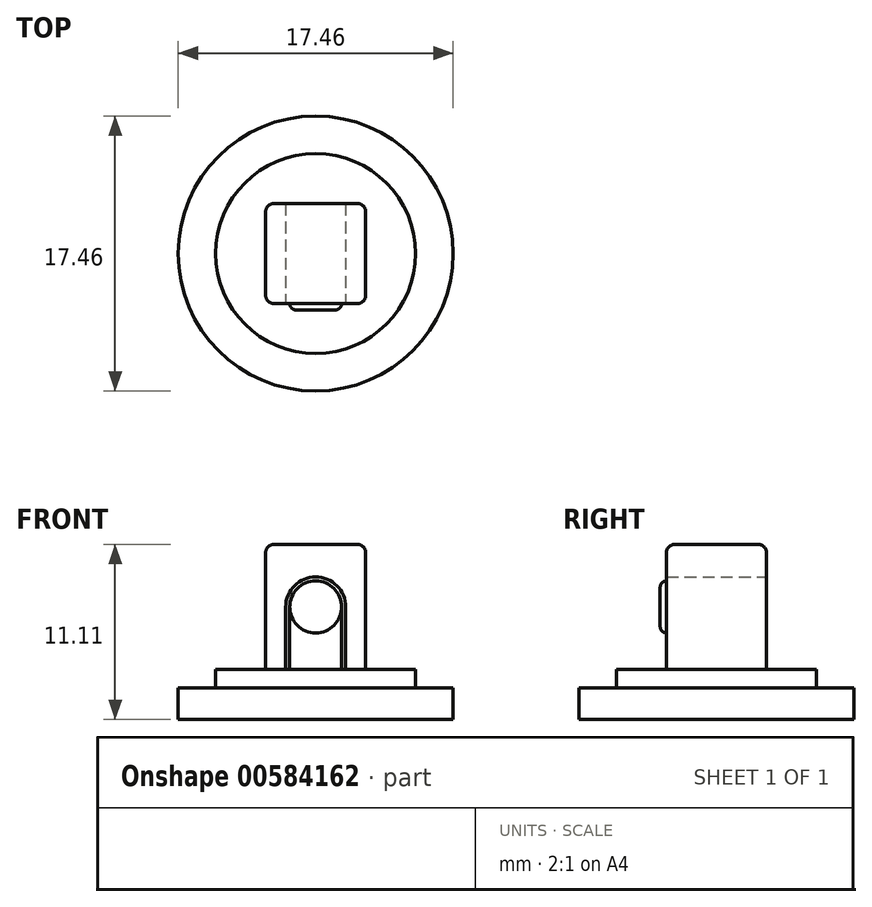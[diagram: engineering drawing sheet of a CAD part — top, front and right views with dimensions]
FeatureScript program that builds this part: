
annotation { "Feature Type Name" : "Feature", "Feature Type Description" : "" }
export const myFeature = defineFeature(function(context is Context, id is Id, definition is map)
    precondition{}
    {
        {
            var Q0;
            Q0=qCreatedBy(makeId("Top.planeOp"),FACE);
            var sketch = newSketch(context, id + "F0", { "sketchPlane" : qUnion([Q0])});
            skCircle(sketch, "E0", {"center": v(0, 0) * mm, "radius": 8.73 * mm});
            skSolve(sketch);
        }
        {
            var Q0;
            Q0=qSketchRegion(id+"F0",true);
            extrude(context, id + "F1", {"entities" : qUnion([Q0]), "depth" : 1.98 * mm, "offsetDistance" : 25.4 * mm});
        }
        {
            var Q0;
            Q0=makeQuery(id+"F1.opExtrude","CAP_FACE",FACE,{"disambiguationData":[OSD([sQuery(id+"F0.wireOp",EDGE,"E0")])],"isStart":false});
            var sketch = newSketch(context, id + "F2", { "sketchPlane" : qUnion([Q0])});
            skCircle(sketch, "E1", {"center": v(0, 0) * mm, "radius": 6.35 * mm});
            skSolve(sketch);
        }
        {
            var Q0;
            Q0=qSketchRegion(id+"F2",true);
            extrude(context, id + "F3", {"entities" : qUnion([Q0]), "operationType" : NewBodyOperationType.ADD, "depth" : 1.2 * mm, "offsetDistance" : 25.4 * mm});
        }
        {
            var Q0;
            Q0=makeQuery(id+"F3.opExtrude","CAP_FACE",FACE,{"disambiguationData":[OSD([sQuery(id+"F2.wireOp",EDGE,"E1")])],"isStart":false});
            var sketch = newSketch(context, id + "F4", { "sketchPlane" : qUnion([Q0])});
            skLineSegment(sketch, "E2.bottom", {"start": v(3.18, 3.18) * mm, "end": v(-3.18, 3.18) * mm});
            skLineSegment(sketch, "E2.top", {"start": v(3.18, -3.18) * mm, "end": v(-3.18, -3.18) * mm});
            skLineSegment(sketch, "E2.left", {"start": v(3.18, 3.18) * mm, "end": v(3.18, -3.18) * mm});
            skLineSegment(sketch, "E2.right", {"start": v(-3.18, 3.18) * mm, "end": v(-3.18, -3.18) * mm});
            skPoint(sketch, "E2.middle", {"position": v(0, 0) * mm});
            skSolve(sketch);
        }
        {
            var Q0;
            Q0=qSketchRegion(id+"F4",true);
            extrude(context, id + "F5", {"entities" : qUnion([Q0]), "operationType" : NewBodyOperationType.ADD, "depth" : 7.94 * mm, "offsetDistance" : 25.4 * mm});
        }
        {
            var Q0;
            Q0=qCreatedBy(makeId("Front.planeOp"),FACE);
            var sketch = newSketch(context, id + "F6", { "sketchPlane" : qUnion([Q0])});
            skCircle(sketch, "E3", {"center": v(0, 7.14) * mm, "radius": 1.9 * mm});
            skSolve(sketch);
        }
        {
            var Q0;
            Q0=qSketchRegion(id+"F6",true);
            extrude(context, id + "F7", {"entities" : qUnion([Q0]), "operationType" : NewBodyOperationType.REMOVE, "endBound" : BoundingType.THROUGH_ALL, "depth" : 25.4 * mm, "offsetDistance" : 25.4 * mm, "hasSecondDirection" : true, "secondDirectionBound" : SecondDirectionBoundingType.THROUGH_ALL, "secondDirectionOppositeDirection" : true, "secondDirectionDepth" : 25.4 * mm});
        }
        {
            var Q0;
            Q0=makeQuery(id+"F5.opExtrude","SWEPT_FACE",FACE,{"disambiguationData":[OSD([sQuery(id+"F4.wireOp",EDGE,"E2.top")])]});
            var sketch = newSketch(context, id + "F8", { "sketchPlane" : qUnion([Q0])});
            skLineSegment(sketch, "E4.bottom", {"start": v(-1.9, 3.17) * mm, "end": v(1.9, 3.17) * mm});
            skLineSegment(sketch, "E4.left", {"start": v(-1.9, 3.18) * mm, "end": v(-1.9, 7.14) * mm});
            skLineSegment(sketch, "E4.right", {"start": v(1.9, 3.18) * mm, "end": v(1.9, 7.14) * mm});
            skLineSegment(sketch, "E5", {"start": v(-1.9, 7.14) * mm, "end": v(1.9, 7.14) * mm});
            skSolve(sketch);
        }
        {
            var Q0;
            Q0=qSketchRegion(id+"F8",true);
            extrude(context, id + "F9", {"entities" : qUnion([Q0]), "operationType" : NewBodyOperationType.REMOVE, "endBound" : BoundingType.THROUGH_ALL, "oppositeDirection" : true, "depth" : 25.4 * mm, "offsetDistance" : 25.4 * mm});
        }
        {
            var Q0;
            Q0=makeQuery(id+"F5.opExtrude","SWEPT_FACE",FACE,{"disambiguationData":[OSD([sQuery(id+"F4.wireOp",EDGE,"E2.top")])]});
            var sketch = newSketch(context, id + "F10", { "sketchPlane" : qUnion([Q0])});
            skArc(sketch, "E6", {"start": v(1.65, 7.14) * mm, "mid": v(0, 8.8) * mm, "end": v(-1.65, 7.14) * mm});
            skLineSegment(sketch, "E7.bottom", {"start": v(-1.65, 3.17) * mm, "end": v(1.65, 3.17) * mm});
            skLineSegment(sketch, "E7.left", {"start": v(-1.65, 3.18) * mm, "end": v(-1.65, 7.14) * mm});
            skLineSegment(sketch, "E7.right", {"start": v(1.65, 3.18) * mm, "end": v(1.65, 7.14) * mm});
            skSolve(sketch);
        }
        {
            var Q0;
            Q0=qSketchRegion(id+"F10",true);
            extrude(context, id + "F11", {"entities" : qUnion([Q0]), "operationType" : NewBodyOperationType.ADD, "oppositeDirection" : true, "depth" : 1 / 812.8 * mm, "offsetDistance" : 25.4 * mm});
        }
        {
            var Q0;
            Q0=makeQuery(id+"F11.opExtrude","CAP_FACE",FACE,{"disambiguationData":[OSD([sQuery(id+"F10.wireOp",EDGE,"E6"),sQuery(id+"F10.wireOp",EDGE,"E7.bottom"),sQuery(id+"F10.wireOp",EDGE,"E7.left"),sQuery(id+"F10.wireOp",EDGE,"E7.right")])],"isStart":true});
            var sketch = newSketch(context, id + "F12", { "sketchPlane" : qUnion([Q0])});
            skCircle(sketch, "E8", {"center": v(0, 7.14) * mm, "radius": 1.65 * mm});
            skSolve(sketch);
        }
        {
            var Q0;
            Q0=qSketchRegion(id+"F12",true);
            extrude(context, id + "F13", {"entities" : qUnion([Q0]), "operationType" : NewBodyOperationType.ADD, "depth" : 0.4 * mm, "offsetDistance" : 25.4 * mm});
        }
        {
            var Q0;
            Q0=makeQuery(id+"F13.opExtrude","CAP_EDGE",EDGE,{"disambiguationData":[OSD([sQuery(id+"F12.wireOp",EDGE,"E8")])],"isStart":false});
            fillet(context, id + "F14", {"entities" : qUnion([Q0]), "radius" : 0.4 * mm, "tangentPropagation" : true, "allowEdgeOverflow" : false});
        }
        {
            var Q0;
            Q0=makeQuery(id+"F5.opExtrude","CAP_FACE",FACE,{"disambiguationData":[OSD([sQuery(id+"F4.wireOp",EDGE,"E2.bottom"),sQuery(id+"F4.wireOp",EDGE,"E2.top"),sQuery(id+"F4.wireOp",EDGE,"E2.left"),sQuery(id+"F4.wireOp",EDGE,"E2.right")])],"isStart":false});
            var Q1;
            Q1=makeQuery(id+"F5.opExtrude","SWEPT_EDGE",EDGE,{"disambiguationData":[OSD([sQuery(id+"F4.wireOp",EDGE,"E2.top"),sQuery(id+"F4.wireOp",EDGE,"E2.left")])]});
            var Q2;
            Q2=makeQuery(id+"F5.opExtrude","SWEPT_EDGE",EDGE,{"disambiguationData":[OSD([sQuery(id+"F4.wireOp",EDGE,"E2.bottom"),sQuery(id+"F4.wireOp",EDGE,"E2.left")])]});
            var Q3;
            Q3=makeQuery(id+"F5.opExtrude","SWEPT_EDGE",EDGE,{"disambiguationData":[OSD([sQuery(id+"F4.wireOp",EDGE,"E2.top"),sQuery(id+"F4.wireOp",EDGE,"E2.right")])]});
            var Q4;
            Q4=makeQuery(id+"F5.opExtrude","SWEPT_EDGE",EDGE,{"disambiguationData":[OSD([sQuery(id+"F4.wireOp",EDGE,"E2.bottom"),sQuery(id+"F4.wireOp",EDGE,"E2.right")])]});
            fillet(context, id + "F15", {"entities" : qUnion([Q0, Q1, Q2, Q3, Q4]), "radius" : 0.5 * mm, "tangentPropagation" : true, "allowEdgeOverflow" : false});
        }
    });
